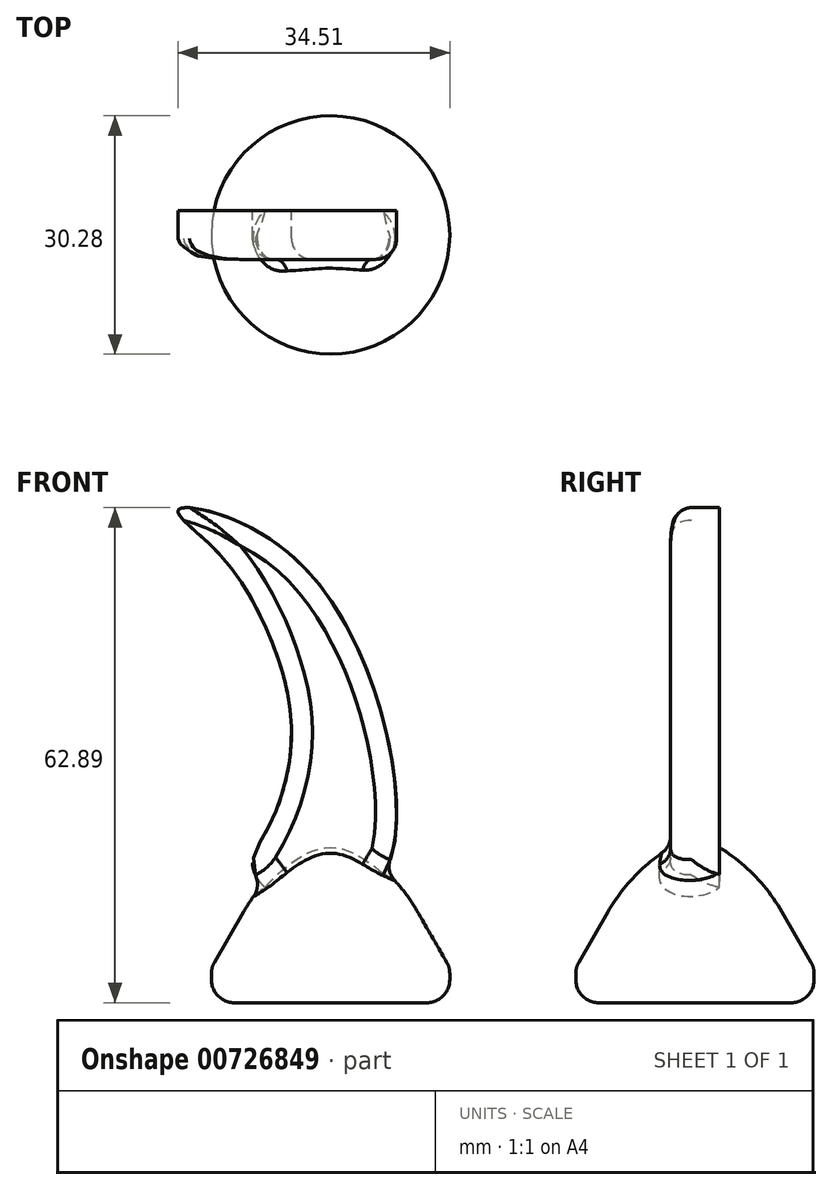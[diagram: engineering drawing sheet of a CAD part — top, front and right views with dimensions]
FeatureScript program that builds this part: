
annotation { "Feature Type Name" : "Feature", "Feature Type Description" : "" }
export const myFeature = defineFeature(function(context is Context, id is Id, definition is map)
    precondition{}
    {
        {
            var Q0;
            Q0=qCreatedBy(makeId("Front.planeOp"),FACE);
            var sketch = newSketch(context, id + "F0", { "sketchPlane" : qUnion([Q0])});
            skLineSegment(sketch, "E0", {"start": v(0, 0) * mm, "end": v(-15.14, 0) * mm});
            skLineSegment(sketch, "E1", {"start": v(-15.14, 0) * mm, "end": v(-15.14, 4.46) * mm});
            skLineSegment(sketch, "E2", {"start": v(-15.14, 4.46) * mm, "end": v(-7.96, 16.89) * mm});
            skLineSegment(sketch, "E3", {"start": v(-7.96, 16.89) * mm, "end": v(-2.01, 20.39) * mm});
            skLineSegment(sketch, "E4", {"start": v(-2.01, 20.39) * mm, "end": v(0, 20.39) * mm});
            skLineSegment(sketch, "E5", {"start": v(0, 20.39) * mm, "end": v(0, 0) * mm});
            skSolve(sketch);
        }
        {
            var Q0;
            Q0 = qSketchRegion(id + "F0", true);
            var Q1;
            Q1=sQuery(id+"F0.wireOp",EDGE,"E5");
            revolve(context, id + "F1", {"surfaceOperationType" : NewSurfaceOperationType.NEW, "entities" : qUnion([Q0]), "axis" : qUnion([Q1]), "revolveType" : RevolveType.FULL});
        }
        {
            var Q0;
            Q0=makeQuery(id+"F1.opRevolve","SWEPT_EDGE",EDGE,{"disambiguationData":[OSD([sQuery(id+"F0.wireOp",EDGE,"E2"),sQuery(id+"F0.wireOp",EDGE,"E3")])]});
            fillet(context, id + "F2", {"entities" : qUnion([Q0]), "radius" : 23.43 * mm, "tangentPropagation" : true, "allowEdgeOverflow" : false});
        }
        {
            var Q0;
            Q0=makeQuery(id+"F1.opRevolve","SWEPT_FACE",FACE,{"disambiguationData":[OSD([sQuery(id+"F0.wireOp",EDGE,"E1")])]});
            fillet(context, id + "F3", {"entities" : qUnion([Q0]), "radius" : 2.9 * mm, "tangentPropagation" : true, "allowEdgeOverflow" : false});
        }
        {
            var Q0;
            Q0=qCreatedBy(makeId("Front.planeOp"),FACE);
            var sketch = newSketch(context, id + "F4", { "sketchPlane" : qUnion([Q0])});
            skFitSpline(sketch, "E6", {"points": [v(-6.04, 13.21) * mm, v(4.46, 13.91) * mm, v(8.31, 26.34) * mm, v(-5.51, 57.31) * mm, v(-19.34, 62.56) * mm, v(-15.49, 58.36) * mm, v(-9.54, 50.31) * mm, v(-4.99, 35.44) * mm, v(-7.79, 22.49) * mm, v(-9.89, 17.41) * mm, v(-6.04, 13.21) * mm]});
            skSolve(sketch);
        }
        {
            var Q0;
            Q0=makeQuery(id+"F4.imprint","IMPRINT",FACE,{"disambiguationData":[TD([[makeQuery(id+"F4.imprint","IMPRINT",EDGE,{"derivedFrom":sQuery(id+"F4.wireOp",EDGE,"E6")}),1.0]])]});
            extrude(context, id + "F5", {"entities" : qUnion([Q0]), "operationType" : NewBodyOperationType.ADD, "endBound" : BoundingType.SYMMETRIC, "depth" : 6.2 * mm, "offsetDistance" : 25 * mm});
        }
        {
            var Q0;
            Q0=makeQuery(id+"F5.opExtrude","CAP_FACE",FACE,{"disambiguationData":[OSD([sQuery(id+"F4.wireOp",EDGE,"E6")])],"isStart":false});
            fillet(context, id + "F6", {"entities" : qUnion([Q0]), "radius" : 2.66 * mm, "allowEdgeOverflow" : false});
        }
    });
